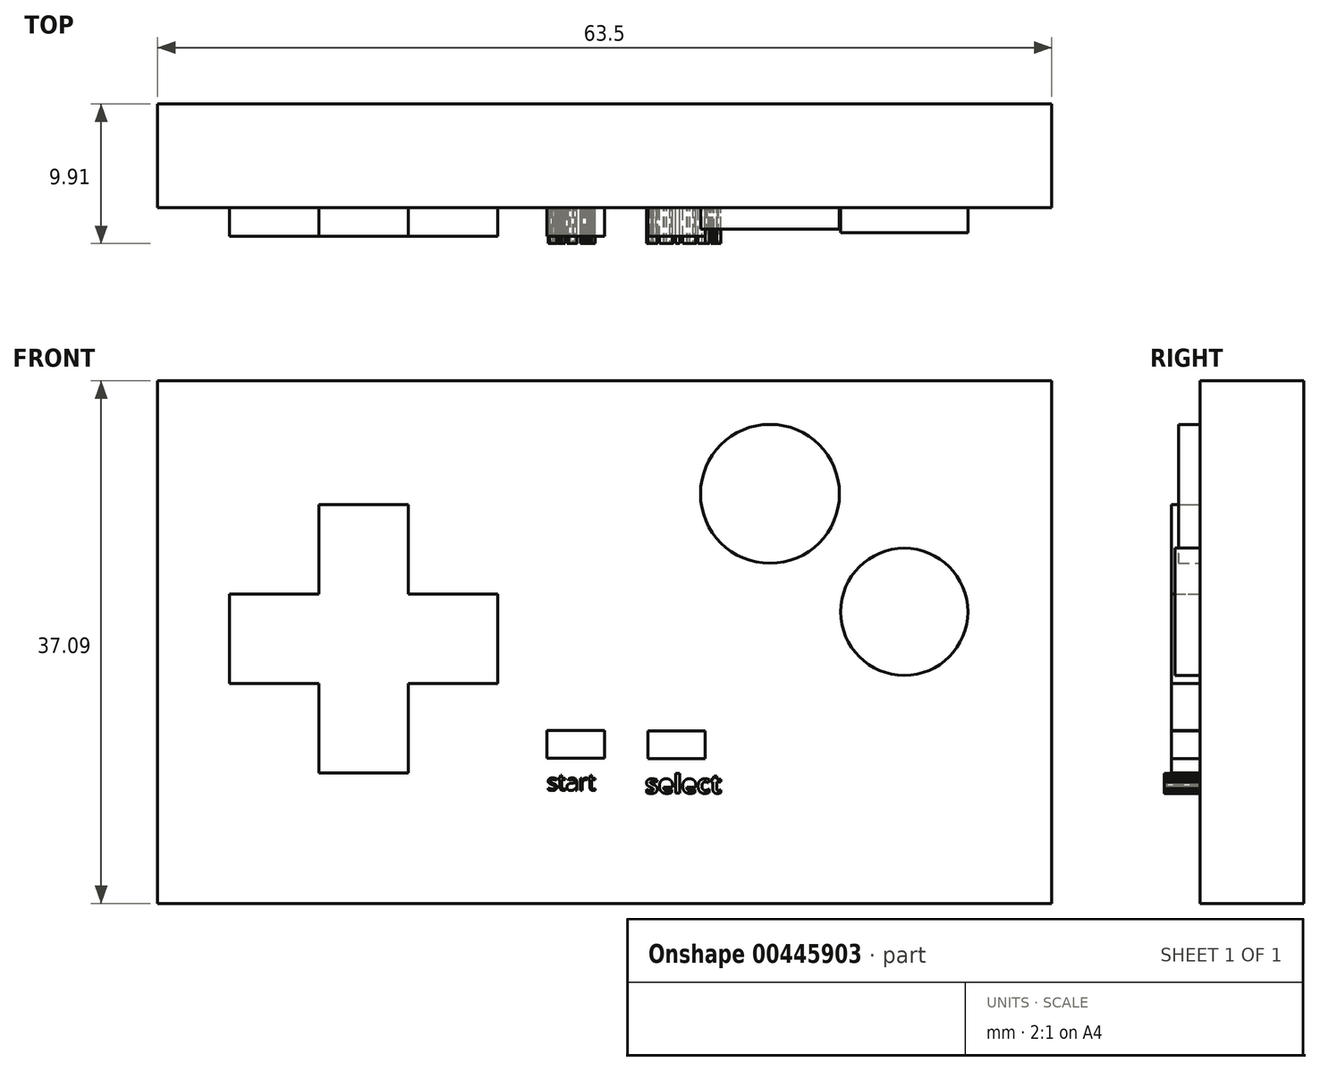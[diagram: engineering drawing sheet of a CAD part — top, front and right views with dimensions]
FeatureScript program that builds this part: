
annotation { "Feature Type Name" : "Feature", "Feature Type Description" : "" }
export const myFeature = defineFeature(function(context is Context, id is Id, definition is map)
    precondition{}
    {
        {
            var Q0;
            Q0=qCreatedBy(makeId("Front.planeOp"),FACE);
            var sketch = newSketch(context, id + "F0", { "sketchPlane" : qUnion([Q0])});
            skLineSegment(sketch, "E0.bottom", {"start": v(0, 0) * mm, "end": v(63.5, 0) * mm});
            skLineSegment(sketch, "E0.top", {"start": v(0, 37.1) * mm, "end": v(63.5, 37.1) * mm});
            skLineSegment(sketch, "E0.left", {"start": v(0, 0) * mm, "end": v(0, 37.1) * mm});
            skLineSegment(sketch, "E0.right", {"start": v(63.5, 0) * mm, "end": v(63.5, 37.1) * mm});
            skCircle(sketch, "E1", {"center": v(43.5, 29.07) * mm, "radius": 4.93 * mm});
            skCircle(sketch, "E2", {"center": v(53.03, 20.7) * mm, "radius": 4.52 * mm});
            skSolve(sketch);
        }
        {
            var Q0;
            Q0 = qSketchRegion(id + "F0", true);
            extrude(context, id + "F1", {"entities" : qUnion([Q0]), "depth" : 7.37 * mm});
        }
        {
            var Q0;
            Q0=qCreatedBy(makeId("Front.planeOp"),FACE);
            var sketch = newSketch(context, id + "F2", { "sketchPlane" : qUnion([Q0])});
            skSolve(sketch);
        }
        {
            var Q0;
            Q0 = qSketchRegion(id + "F2", true);
            var Q1;
            Q1=makeQuery(id+"F0.imprint","IMPRINT",FACE,{"disambiguationData":[TD([[makeQuery(id+"F0.imprint","IMPRINT",EDGE,{"derivedFrom":sQuery(id+"F0.wireOp",EDGE,"E1")}),1.0]])]});
            extrude(context, id + "F3", {"entities" : qUnion([Q0, Q1]), "operationType" : NewBodyOperationType.ADD, "depth" : 8.9 * mm});
        }
        {
            var Q0;
            Q0=makeQuery(id+"F0.imprint","IMPRINT",FACE,{"disambiguationData":[TD([[makeQuery(id+"F0.imprint","IMPRINT",EDGE,{"derivedFrom":sQuery(id+"F0.wireOp",EDGE,"E2")}),1.0]])]});
            extrude(context, id + "F4", {"entities" : qUnion([Q0]), "operationType" : NewBodyOperationType.ADD, "depth" : 9.14 * mm});
        }
        {
            var Q0;
            Q0=qCreatedBy(makeId("Front.planeOp"),FACE);
            var sketch = newSketch(context, id + "F5", { "sketchPlane" : qUnion([Q0])});
            skLineSegment(sketch, "E3", {"start": v(11.46, 28.32) * mm, "end": v(11.46, 21.97) * mm});
            skLineSegment(sketch, "E4", {"start": v(11.46, 28.32) * mm, "end": v(17.8, 28.32) * mm});
            skLineSegment(sketch, "E5", {"start": v(17.8, 28.32) * mm, "end": v(17.8, 21.97) * mm});
            skLineSegment(sketch, "E6", {"start": v(17.8, 21.97) * mm, "end": v(24.16, 21.97) * mm});
            skLineSegment(sketch, "E7", {"start": v(24.16, 21.97) * mm, "end": v(24.16, 15.62) * mm});
            skLineSegment(sketch, "E8", {"start": v(24.16, 15.62) * mm, "end": v(17.8, 15.62) * mm});
            skLineSegment(sketch, "E9", {"start": v(17.8, 15.62) * mm, "end": v(17.8, 9.27) * mm});
            skLineSegment(sketch, "E10", {"start": v(17.8, 9.27) * mm, "end": v(11.46, 9.27) * mm});
            skLineSegment(sketch, "E11", {"start": v(11.46, 9.27) * mm, "end": v(11.46, 15.62) * mm});
            skLineSegment(sketch, "E12", {"start": v(11.46, 15.62) * mm, "end": v(5.1, 15.62) * mm});
            skLineSegment(sketch, "E13", {"start": v(5.1, 15.62) * mm, "end": v(5.1, 21.97) * mm});
            skLineSegment(sketch, "E14", {"start": v(5.1, 21.97) * mm, "end": v(11.46, 21.97) * mm});
            skLineSegment(sketch, "E15.bottom", {"start": v(27.66, 12.27) * mm, "end": v(31.75, 12.27) * mm});
            skLineSegment(sketch, "E15.top", {"start": v(27.66, 10.3) * mm, "end": v(31.75, 10.3) * mm});
            skLineSegment(sketch, "E15.left", {"start": v(27.66, 12.27) * mm, "end": v(27.66, 10.3) * mm});
            skLineSegment(sketch, "E15.right", {"start": v(31.75, 12.27) * mm, "end": v(31.75, 10.3) * mm});
            skLineSegment(sketch, "E16.bottom", {"start": v(34.82, 12.24) * mm, "end": v(38.9, 12.24) * mm});
            skLineSegment(sketch, "E16.top", {"start": v(34.82, 10.27) * mm, "end": v(38.9, 10.27) * mm});
            skLineSegment(sketch, "E16.left", {"start": v(34.82, 12.24) * mm, "end": v(34.82, 10.27) * mm});
            skLineSegment(sketch, "E16.right", {"start": v(38.9, 12.24) * mm, "end": v(38.9, 10.27) * mm});
            skSolve(sketch);
        }
        {
            var Q0;
            Q0=makeQuery(id+"F5.imprint","IMPRINT",FACE,{"disambiguationData":[TD([[makeQuery(id+"F5.imprint","IMPRINT",EDGE,{"derivedFrom":sQuery(id+"F5.wireOp",EDGE,"E16.bottom")}),-1.0]])]});
            var Q1;
            Q1=makeQuery(id+"F5.imprint","IMPRINT",FACE,{"disambiguationData":[TD([[makeQuery(id+"F5.imprint","IMPRINT",EDGE,{"derivedFrom":sQuery(id+"F5.wireOp",EDGE,"E3")}),1.0]])]});
            var Q2;
            Q2=makeQuery(id+"F5.imprint","IMPRINT",FACE,{"disambiguationData":[TD([[makeQuery(id+"F5.imprint","IMPRINT",EDGE,{"derivedFrom":sQuery(id+"F5.wireOp",EDGE,"E15.bottom")}),-1.0]])]});
            extrude(context, id + "F6", {"entities" : qUnion([Q0, Q1, Q2]), "operationType" : NewBodyOperationType.ADD, "depth" : 9.4 * mm});
        }
        {
            var Q0;
            Q0=makeQuery(id+"F1.opExtrude","CAP_FACE",FACE,{"disambiguationData":[OSD([sQuery(id+"F0.wireOp",EDGE,"E0.bottom"),sQuery(id+"F0.wireOp",EDGE,"E0.top"),sQuery(id+"F0.wireOp",EDGE,"E0.left"),sQuery(id+"F0.wireOp",EDGE,"E0.right"),sQuery(id+"F0.wireOp",EDGE,"E1"),sQuery(id+"F0.wireOp",EDGE,"E2")])],"isStart":false});
            var sketch = newSketch(context, id + "F7", { "sketchPlane" : qUnion([Q0])});
            skText(sketch, "E17", { "text": "start", "fontName": "OpenSans-Regular.ttf"});
            skText(sketch, "E18", { "text": "select", "fontName": "OpenSans-Bold.ttf"});
            const initialGuessF7  = {"E17": [0.02766, 0.00803, 1, 0, 0.00116], "E18": [0.03464, 0.00782, 1, 0, 0.00133]};
            skSetInitialGuess(sketch, initialGuessF7);
            skSolve(sketch);
        }
        {
            var Q0;
            Q0=qCreatedBy(makeId("Front.planeOp"),FACE);
            var sketch = newSketch(context, id + "F8", { "sketchPlane" : qUnion([Q0])});
            skSolve(sketch);
        }
        {
            var Q0;
            Q0 = qSketchRegion(id + "F8", true);
            var Q1;
            Q1=makeQuery(id+"F7.imprint","IMPRINT",FACE,{"disambiguationData":[TD([[makeQuery(id+"F7.imprint","IMPRINT",EDGE,{"derivedFrom":sQuery(id+"F7.wireOp",EDGE,"E18.sketch_text.stroke-84")}),-1.0]])]});
            var Q2;
            Q2=makeQuery(id+"F7.imprint","IMPRINT",FACE,{"disambiguationData":[TD([[makeQuery(id+"F7.imprint","IMPRINT",EDGE,{"derivedFrom":sQuery(id+"F7.wireOp",EDGE,"E18.sketch_text.stroke-70")}),-1.0]])]});
            var Q3;
            Q3=makeQuery(id+"F7.imprint","IMPRINT",FACE,{"disambiguationData":[TD([[makeQuery(id+"F7.imprint","IMPRINT",EDGE,{"derivedFrom":sQuery(id+"F7.wireOp",EDGE,"E18.sketch_text.stroke-0")}),-1.0]])]});
            var Q4;
            Q4=makeQuery(id+"F7.imprint","IMPRINT",FACE,{"disambiguationData":[TD([[makeQuery(id+"F7.imprint","IMPRINT",EDGE,{"derivedFrom":sQuery(id+"F7.wireOp",EDGE,"E18.sketch_text.stroke-50")}),-1.0]])]});
            var Q5;
            Q5=makeQuery(id+"F7.imprint","IMPRINT",FACE,{"disambiguationData":[TD([[makeQuery(id+"F7.imprint","IMPRINT",EDGE,{"derivedFrom":sQuery(id+"F7.wireOp",EDGE,"E17.sketch_text.stroke-0")}),-1.0]])]});
            var Q6;
            Q6=makeQuery(id+"F7.imprint","IMPRINT",FACE,{"disambiguationData":[TD([[makeQuery(id+"F7.imprint","IMPRINT",EDGE,{"derivedFrom":sQuery(id+"F7.wireOp",EDGE,"E18.sketch_text.stroke-26")}),-1.0]])]});
            var Q7;
            Q7=makeQuery(id+"F7.imprint","IMPRINT",FACE,{"disambiguationData":[TD([[makeQuery(id+"F7.imprint","IMPRINT",EDGE,{"derivedFrom":sQuery(id+"F7.wireOp",EDGE,"E18.sketch_text.stroke-50")}),1.0]])]});
            var Q8;
            Q8=makeQuery(id+"F7.imprint","IMPRINT",FACE,{"disambiguationData":[TD([[makeQuery(id+"F7.imprint","IMPRINT",EDGE,{"derivedFrom":sQuery(id+"F7.wireOp",EDGE,"E18.sketch_text.stroke-46")}),-1.0]])]});
            var Q9;
            Q9=makeQuery(id+"F7.imprint","IMPRINT",FACE,{"disambiguationData":[TD([[makeQuery(id+"F7.imprint","IMPRINT",EDGE,{"derivedFrom":sQuery(id+"F7.wireOp",EDGE,"E18.sketch_text.stroke-26")}),1.0]])]});
            var Q10;
            Q10=makeQuery(id+"F7.imprint","IMPRINT",FACE,{"disambiguationData":[TD([[makeQuery(id+"F7.imprint","IMPRINT",EDGE,{"derivedFrom":sQuery(id+"F7.wireOp",EDGE,"E17.sketch_text.stroke-84")}),-1.0]])]});
            var Q11;
            Q11=makeQuery(id+"F7.imprint","IMPRINT",FACE,{"disambiguationData":[TD([[makeQuery(id+"F7.imprint","IMPRINT",EDGE,{"derivedFrom":sQuery(id+"F7.wireOp",EDGE,"E17.sketch_text.stroke-71")}),-1.0]])]});
            var Q12;
            Q12=makeQuery(id+"F7.imprint","IMPRINT",FACE,{"disambiguationData":[TD([[makeQuery(id+"F7.imprint","IMPRINT",EDGE,{"derivedFrom":sQuery(id+"F7.wireOp",EDGE,"E17.sketch_text.stroke-63")}),1.0]])]});
            var Q13;
            Q13=makeQuery(id+"F7.imprint","IMPRINT",FACE,{"disambiguationData":[TD([[makeQuery(id+"F7.imprint","IMPRINT",EDGE,{"derivedFrom":sQuery(id+"F7.wireOp",EDGE,"E17.sketch_text.stroke-25")}),-1.0]])]});
            var Q14;
            Q14=makeQuery(id+"F7.imprint","IMPRINT",FACE,{"disambiguationData":[TD([[makeQuery(id+"F7.imprint","IMPRINT",EDGE,{"derivedFrom":sQuery(id+"F7.wireOp",EDGE,"E17.sketch_text.stroke-44")}),-1.0]])]});
            extrude(context, id + "F9", {"entities" : qUnion([Q0, Q1, Q2, Q3, Q4, Q5, Q6, Q7, Q8, Q9, Q10, Q11, Q12, Q13, Q14]), "operationType" : NewBodyOperationType.ADD, "depth" : 2.54 * mm});
        }
    });
